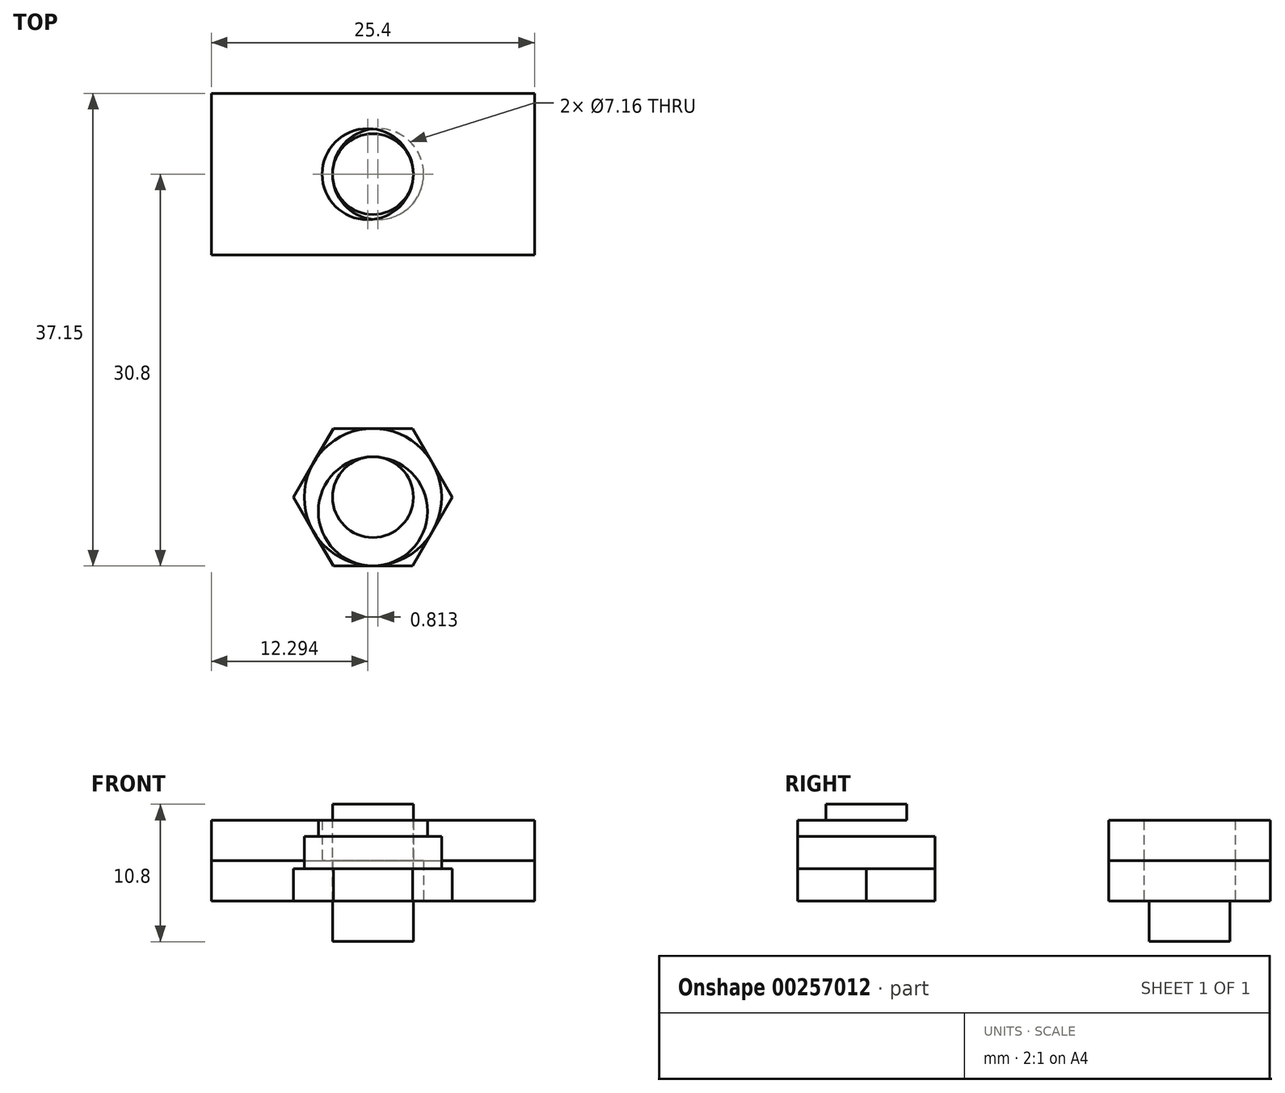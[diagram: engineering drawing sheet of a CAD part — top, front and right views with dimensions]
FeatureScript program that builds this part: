
annotation { "Feature Type Name" : "Feature", "Feature Type Description" : "" }
export const myFeature = defineFeature(function(context is Context, id is Id, definition is map)
    precondition{}
    {
        {
            var Q0;
            Q0=qCreatedBy(makeId("Top.planeOp"),FACE);
            var sketch = newSketch(context, id + "F0", { "sketchPlane" : qUnion([Q0])});
            skLineSegment(sketch, "E0.bottom", {"start": v(-12.7, 6.35) * mm, "end": v(12.7, 6.35) * mm});
            skLineSegment(sketch, "E0.top", {"start": v(-12.7, -6.35) * mm, "end": v(12.7, -6.35) * mm});
            skLineSegment(sketch, "E0.left", {"start": v(-12.7, 6.35) * mm, "end": v(-12.7, -6.35) * mm});
            skLineSegment(sketch, "E0.right", {"start": v(12.7, 6.35) * mm, "end": v(12.7, -6.35) * mm});
            skLineSegment(sketch, "E1", {"start": v(0, 6.35) * mm, "end": v(0, -6.35) * mm});
            skLineSegment(sketch, "E2", {"start": v(12.7, 0) * mm, "end": v(-12.7, 0) * mm});
            skPoint(sketch, "E3", {"position": v(0, 0) * mm});
            skCircle(sketch, "E4", {"center": v(0.4, 0) * mm, "radius": 3.58 * mm});
            skSolve(sketch);
        }
        {
            var Q0;
            Q0=qSketchRegion(id+"F0",true);
            extrude(context, id + "F1", {"entities" : qUnion([Q0]), "depth" : 3.17 * mm});
        }
        {
            var Q0;
            Q0=makeQuery(id+"F1.opExtrude","CAP_FACE",FACE,{"disambiguationData":[OSD([sQuery(id+"F0.wireOp",EDGE,"E0.bottom"),sQuery(id+"F0.wireOp",EDGE,"E0.top"),sQuery(id+"F0.wireOp",EDGE,"E0.left"),sQuery(id+"F0.wireOp",EDGE,"E0.right"),sQuery(id+"F0.wireOp",EDGE,"E4")])],"isStart":false});
            var sketch = newSketch(context, id + "F2", { "sketchPlane" : qUnion([Q0])});
            skLineSegment(sketch, "E5.bottom", {"start": v(-12.7, 6.35) * mm, "end": v(12.7, 6.35) * mm});
            skLineSegment(sketch, "E5.top", {"start": v(-12.7, -6.35) * mm, "end": v(12.7, -6.35) * mm});
            skLineSegment(sketch, "E5.left", {"start": v(-12.7, 6.35) * mm, "end": v(-12.7, -6.35) * mm});
            skLineSegment(sketch, "E5.right", {"start": v(12.7, 6.35) * mm, "end": v(12.7, -6.35) * mm});
            skCircle(sketch, "E6", {"center": v(-0.4, 0) * mm, "radius": 3.58 * mm});
            skSolve(sketch);
        }
        {
            var Q0;
            Q0=qSketchRegion(id+"F2",true);
            extrude(context, id + "F3", {"entities" : qUnion([Q0]), "depth" : 3.17 * mm});
        }
        {
            var Q0;
            Q0=makeQuery(id+"F3.opExtrude","CAP_FACE",FACE,{"disambiguationData":[OSD([sQuery(id+"F2.wireOp",EDGE,"E5.bottom"),sQuery(id+"F2.wireOp",EDGE,"E5.top"),sQuery(id+"F2.wireOp",EDGE,"E5.left"),sQuery(id+"F2.wireOp",EDGE,"E5.right"),sQuery(id+"F2.wireOp",EDGE,"E6")])],"isStart":false});
            var sketch = newSketch(context, id + "F4", { "sketchPlane" : qUnion([Q0])});
            skCircle(sketch, "E7", {"center": v(0, 0) * mm, "radius": 3.17 * mm});
            skSolve(sketch);
        }
        {
            var Q0;
            Q0=qSketchRegion(id+"F4",true);
            extrude(context, id + "F5", {"entities" : qUnion([Q0]), "oppositeDirection" : true, "depth" : 9.52 * mm});
        }
        {
            var Q0;
            Q0=qCreatedBy(makeId("Top.planeOp"),FACE);
            var sketch = newSketch(context, id + "F6", { "sketchPlane" : qUnion([Q0])});
            skCircle(sketch, "E8.cCircle", {"center": v(0, -25.4) * mm, "radius": 5.4 * mm, "construction": true});
            skLineSegment(sketch, "E8.0", {"start": v(6.23, -25.4) * mm, "end": v(3.12, -30.8) * mm});
            skLineSegment(sketch, "E8.1", {"start": v(3.12, -30.8) * mm, "end": v(-3.12, -30.8) * mm});
            skLineSegment(sketch, "E8.2", {"start": v(-3.12, -30.8) * mm, "end": v(-6.23, -25.4) * mm});
            skLineSegment(sketch, "E8.3", {"start": v(-6.23, -25.4) * mm, "end": v(-3.12, -20) * mm});
            skLineSegment(sketch, "E8.4", {"start": v(-3.12, -20) * mm, "end": v(3.12, -20) * mm});
            skLineSegment(sketch, "E8.5", {"start": v(3.12, -20) * mm, "end": v(6.23, -25.4) * mm});
            skPoint(sketch, "E8.0.midPoint", {"position": v(4.67, -28.1) * mm});
            skSolve(sketch);
        }
        {
            var Q0;
            Q0=makeQuery(id+"F6.imprint","IMPRINT",FACE,{"disambiguationData":[TD([[makeQuery(id+"F6.imprint","IMPRINT",EDGE,{"derivedFrom":sQuery(id+"F6.wireOp",EDGE,"E8.0")}),-1.0]])]});
            extrude(context, id + "F7", {"entities" : qUnion([Q0]), "depth" : 2.54 * mm});
        }
        {
            var Q0;
            Q0=makeQuery(id+"F7.opExtrude","CAP_FACE",FACE,{"disambiguationData":[OSD([sQuery(id+"F6.wireOp",EDGE,"E8.0"),sQuery(id+"F6.wireOp",EDGE,"E8.1"),sQuery(id+"F6.wireOp",EDGE,"E8.2"),sQuery(id+"F6.wireOp",EDGE,"E8.3"),sQuery(id+"F6.wireOp",EDGE,"E8.4"),sQuery(id+"F6.wireOp",EDGE,"E8.5")])],"isStart":false});
            var sketch = newSketch(context, id + "F8", { "sketchPlane" : qUnion([Q0])});
            skCircle(sketch, "E9", {"center": v(0, -25.4) * mm, "radius": 5.4 * mm});
            skSolve(sketch);
        }
        {
            var Q0;
            Q0=qSketchRegion(id+"F8",true);
            extrude(context, id + "F9", {"entities" : qUnion([Q0]), "operationType" : NewBodyOperationType.ADD, "depth" : 2.54 * mm});
        }
        {
            var Q0;
            Q0=makeQuery(id+"F9.opExtrude","CAP_FACE",FACE,{"disambiguationData":[OSD([sQuery(id+"F8.wireOp",EDGE,"E9")])],"isStart":false});
            var sketch = newSketch(context, id + "F10", { "sketchPlane" : qUnion([Q0])});
            skCircle(sketch, "E10", {"center": v(0, -25.4) * mm, "radius": 3.18 * mm});
            skSolve(sketch);
        }
        {
            var Q0;
            Q0=makeQuery(id+"F10.imprint","IMPRINT",FACE,{"disambiguationData":[TD([[makeQuery(id+"F10.imprint","IMPRINT",EDGE,{"derivedFrom":sQuery(id+"F10.wireOp",EDGE,"E10")}),1.0]])]});
            extrude(context, id + "F11", {"entities" : qUnion([Q0]), "operationType" : NewBodyOperationType.ADD, "depth" : 2.54 * mm});
        }
        {
            var Q0;
            Q0=makeQuery(id+"F9.opExtrude","CAP_FACE",FACE,{"disambiguationData":[OSD([sQuery(id+"F8.wireOp",EDGE,"E9")])],"isStart":false});
            var sketch = newSketch(context, id + "F12", { "sketchPlane" : qUnion([Q0])});
            skCircle(sketch, "E11", {"center": v(0, -26.51) * mm, "radius": 4.29 * mm});
            skSolve(sketch);
        }
        {
            var Q0;
            Q0=qSketchRegion(id+"F12",true);
            extrude(context, id + "F13", {"entities" : qUnion([Q0]), "operationType" : NewBodyOperationType.ADD, "depth" : 1.27 * mm});
        }
    });
